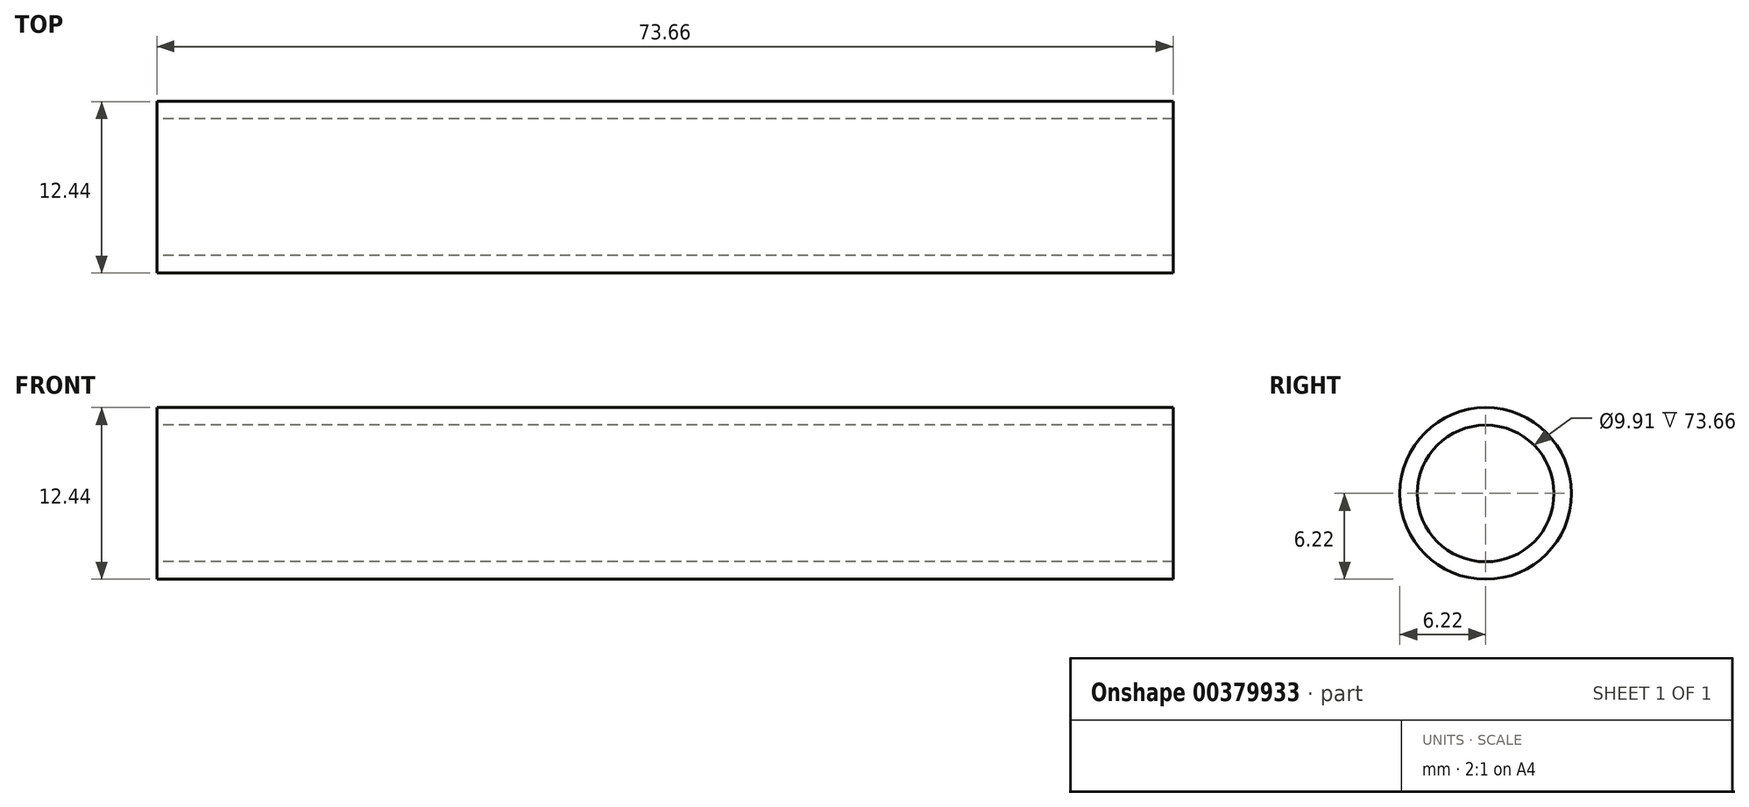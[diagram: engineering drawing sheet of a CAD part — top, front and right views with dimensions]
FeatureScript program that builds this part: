
annotation { "Feature Type Name" : "Feature", "Feature Type Description" : "" }
export const myFeature = defineFeature(function(context is Context, id is Id, definition is map)
    precondition{}
    {
        {
            var Q0;
            Q0=qCreatedBy(makeId("Right.planeOp"),FACE);
            var sketch = newSketch(context, id + "F0", { "sketchPlane" : qUnion([Q0])});
            skCircle(sketch, "E0", {"center": v(0, 0) * mm, "radius": 6.22 * mm});
            skCircle(sketch, "E1", {"center": v(0, 0) * mm, "radius": 4.95 * mm});
            skSolve(sketch);
        }
        {
            var Q0;
            Q0=makeQuery(id+"F0.imprint","IMPRINT",FACE,{"disambiguationData":[TD([[makeQuery(id+"F0.imprint","IMPRINT",EDGE,{"derivedFrom":sQuery(id+"F0.wireOp",EDGE,"E0")}),1.0]])]});
            extrude(context, id + "F1", {"entities" : qUnion([Q0]), "depth" : 73.66 * mm});
        }
    });
